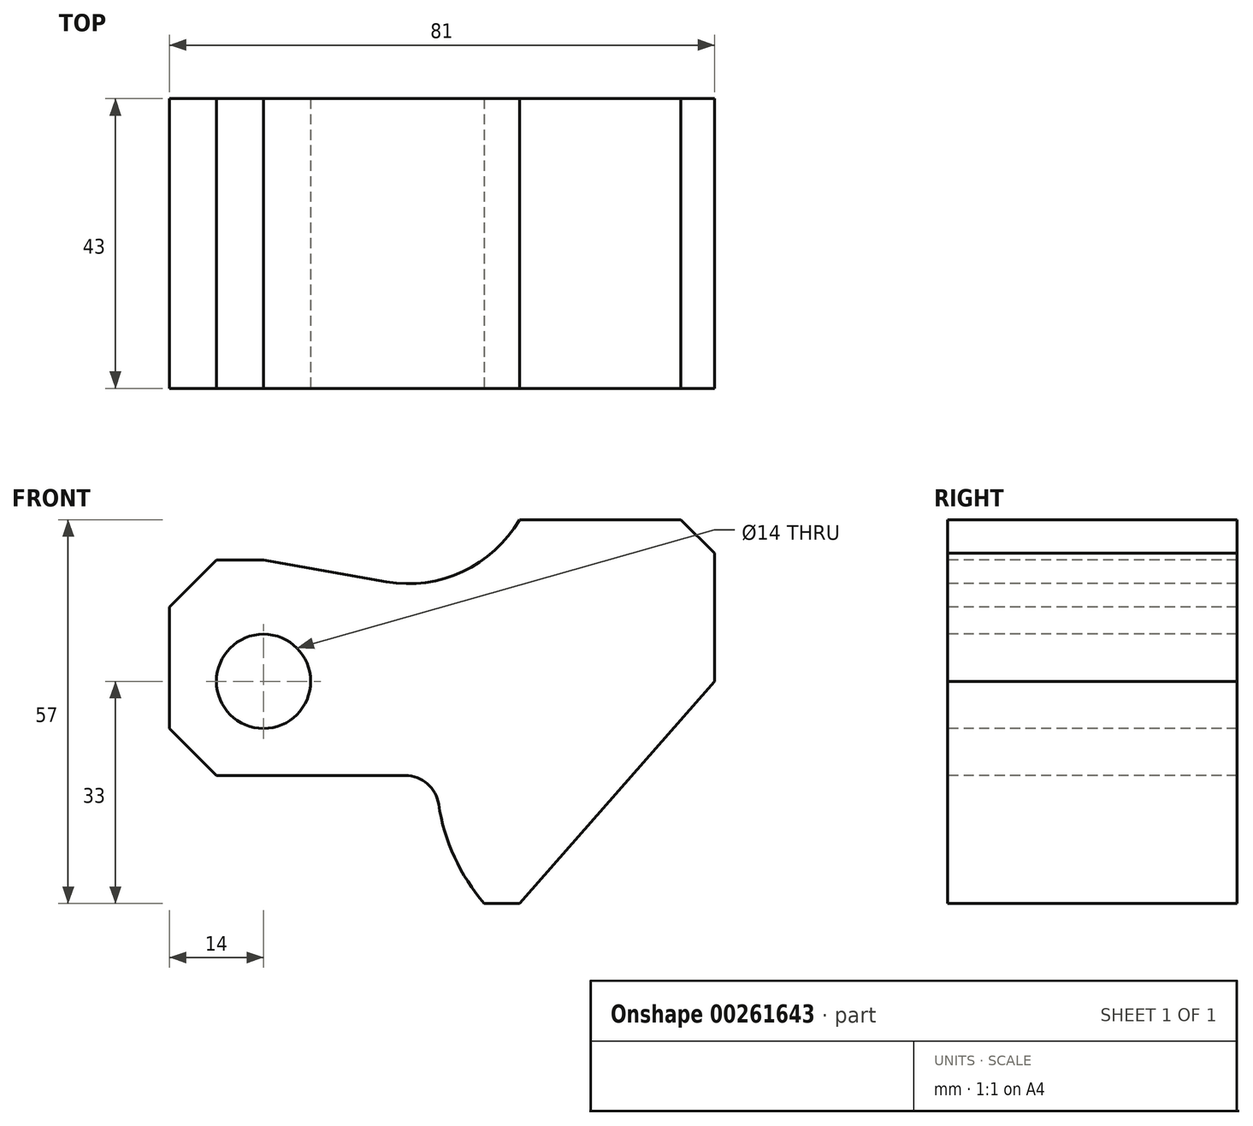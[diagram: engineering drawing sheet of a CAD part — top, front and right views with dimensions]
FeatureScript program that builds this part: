
annotation { "Feature Type Name" : "Feature", "Feature Type Description" : "" }
export const myFeature = defineFeature(function(context is Context, id is Id, definition is map)
    precondition{}
    {
        {
            var Q0;
            Q0=qCreatedBy(makeId("Front.planeOp"),FACE);
            var sketch = newSketch(context, id + "F0", { "sketchPlane" : qUnion([Q0])});
            skCircle(sketch, "E0", {"center": v(0, 0) * mm, "radius": 7 * mm});
            skLineSegment(sketch, "E1", {"start": v(-14, 0) * mm, "end": v(-14, -14) * mm, "construction": true});
            skLineSegment(sketch, "E2", {"start": v(-14, -14) * mm, "end": v(-14, -7) * mm, "construction": true});
            skLineSegment(sketch, "E3", {"start": v(-14, -7) * mm, "end": v(-7, -14) * mm});
            skLineSegment(sketch, "E4", {"start": v(-7, -14) * mm, "end": v(-7, 18) * mm, "construction": true});
            skLineSegment(sketch, "E5", {"start": v(-7, 18) * mm, "end": v(-14, 11) * mm});
            skLineSegment(sketch, "E6", {"start": v(-14, -7) * mm, "end": v(-14, 11) * mm});
            skLineSegment(sketch, "E7", {"start": v(-7, 18) * mm, "end": v(7.38, 18) * mm, "construction": true});
            skArc(sketch, "E8", {"start": v(18.24, 14.78) * mm, "mid": v(29.57, 16.28) * mm, "end": v(38, 24) * mm});
            skLineSegment(sketch, "E9", {"start": v(38, 24) * mm, "end": v(62, 24) * mm});
            skLineSegment(sketch, "E10", {"start": v(62, 24) * mm, "end": v(67, 19) * mm});
            skLineSegment(sketch, "E11", {"start": v(67, 19) * mm, "end": v(67, 0) * mm});
            skLineSegment(sketch, "E12", {"start": v(67, 19) * mm, "end": v(67, 24) * mm, "construction": true});
            skLineSegment(sketch, "E13", {"start": v(67, 0) * mm, "end": v(38, -33) * mm});
            skLineSegment(sketch, "E14", {"start": v(38, -33) * mm, "end": v(67, -33) * mm, "construction": true});
            skLineSegment(sketch, "E15", {"start": v(54.7, -33) * mm, "end": v(54.7, -14) * mm, "construction": true});
            skLineSegment(sketch, "E16", {"start": v(38, -33) * mm, "end": v(32.79, -33) * mm});
            skArc(sketch, "E17", {"start": v(26.01, -18.26) * mm, "mid": v(28.35, -26.12) * mm, "end": v(32.79, -33) * mm});
            skLineSegment(sketch, "E18", {"start": v(-7, -14) * mm, "end": v(21.07, -14) * mm});
            skArc(sketch, "E19", {"start": v(26.01, -18.26) * mm, "mid": v(24.33, -15.21) * mm, "end": v(21.07, -14) * mm});
            skLineSegment(sketch, "E20", {"start": v(-7, 18) * mm, "end": v(0, 18) * mm});
            skLineSegment(sketch, "E21", {"start": v(0, 18) * mm, "end": v(18.24, 14.78) * mm});
            skSolve(sketch);
        }
        {
            var Q0;
            Q0 = qSketchRegion(id + "F0", true);
            extrude(context, id + "F1", {"entities" : qUnion([Q0]), "oppositeDirection" : true, "depth" : 43 * mm});
        }
    });
